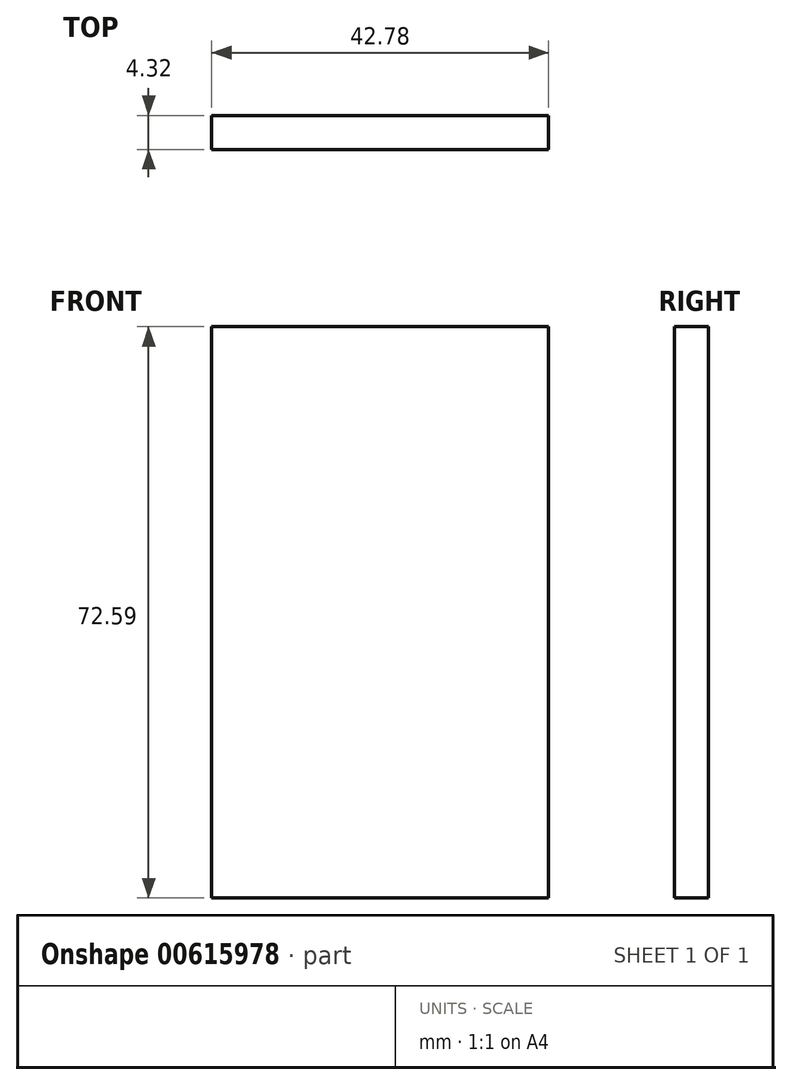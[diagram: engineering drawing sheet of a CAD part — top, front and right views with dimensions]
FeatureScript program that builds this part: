
annotation { "Feature Type Name" : "Feature", "Feature Type Description" : "" }
export const myFeature = defineFeature(function(context is Context, id is Id, definition is map)
    precondition{}
    {
        {
            var Q0;
            Q0=qCreatedBy(makeId("Front.planeOp"),FACE);
            var sketch = newSketch(context, id + "F0", { "sketchPlane" : qUnion([Q0])});
            skLineSegment(sketch, "E0.bottom", {"start": v(0, 0) * mm, "end": v(-42.78, 0) * mm});
            skLineSegment(sketch, "E0.top", {"start": v(0, 72.59) * mm, "end": v(-42.78, 72.59) * mm});
            skLineSegment(sketch, "E0.left", {"start": v(0, 0) * mm, "end": v(0, 72.59) * mm});
            skLineSegment(sketch, "E0.right", {"start": v(-42.78, 0) * mm, "end": v(-42.78, 72.59) * mm});
            skSolve(sketch);
        }
        {
            var Q0;
            Q0 = qSketchRegion(id + "F0", true);
            extrude(context, id + "F1", {"entities" : qUnion([Q0]), "depth" : 4.32 * mm, "offsetDistance" : 25.4 * mm});
        }
    });
